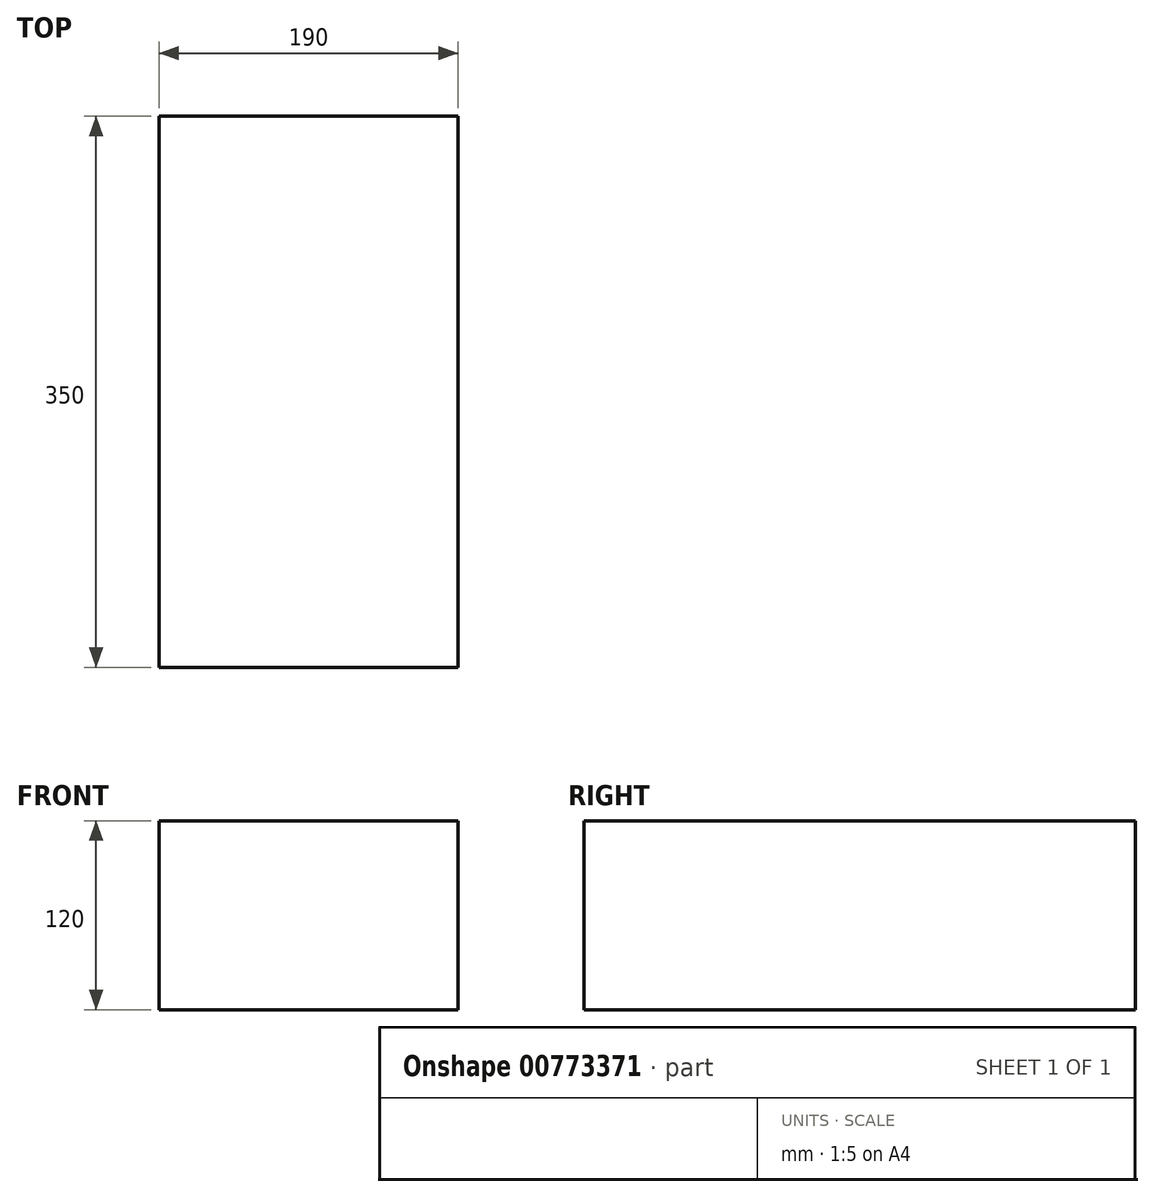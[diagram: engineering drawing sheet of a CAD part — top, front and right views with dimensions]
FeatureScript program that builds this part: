
annotation { "Feature Type Name" : "Feature", "Feature Type Description" : "" }
export const myFeature = defineFeature(function(context is Context, id is Id, definition is map)
    precondition{}
    {
        {
            var Q0;
            Q0=qCreatedBy(makeId("Front.planeOp"),FACE);
            var sketch = newSketch(context, id + "F0", { "sketchPlane" : qUnion([Q0])});
            skLineSegment(sketch, "E0.bottom", {"start": v(-109.2, 62.68) * mm, "end": v(80.8, 62.68) * mm});
            skLineSegment(sketch, "E0.top", {"start": v(-109.2, -57.32) * mm, "end": v(80.8, -57.32) * mm});
            skLineSegment(sketch, "E0.left", {"start": v(-109.2, 62.68) * mm, "end": v(-109.2, -57.32) * mm});
            skLineSegment(sketch, "E0.right", {"start": v(80.8, 62.68) * mm, "end": v(80.8, -57.32) * mm});
            skSolve(sketch);
        }
        {
            var Q0;
            Q0=makeQuery(id+"F0.imprint","IMPRINT",FACE,{"disambiguationData":[TD([[makeQuery(id+"F0.imprint","IMPRINT",EDGE,{"derivedFrom":sQuery(id+"F0.wireOp",EDGE,"E0.bottom")}),-1.0]])]});
            extrude(context, id + "F1", {"entities" : qUnion([Q0]), "depth" : 350 * mm, "offsetDistance" : 25 * mm});
        }
    });
